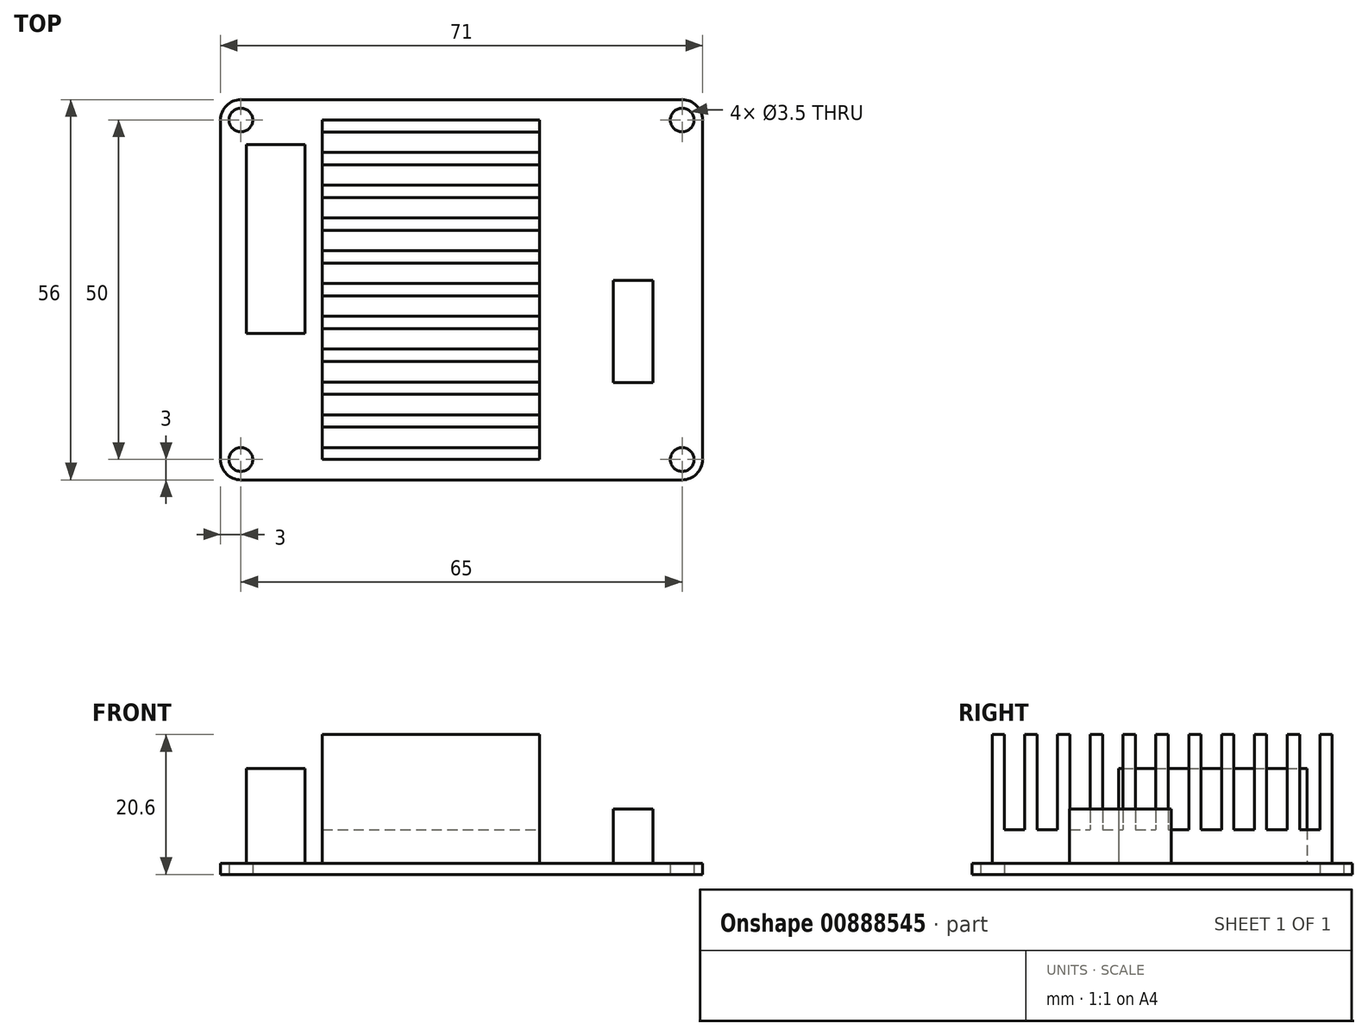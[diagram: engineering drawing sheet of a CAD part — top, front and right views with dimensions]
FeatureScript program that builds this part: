
annotation { "Feature Type Name" : "Feature", "Feature Type Description" : "" }
export const myFeature = defineFeature(function(context is Context, id is Id, definition is map)
    precondition{}
    {
        {
            var Q0;
            Q0=qCreatedBy(makeId("Top.planeOp"),FACE);
            var sketch = newSketch(context, id + "F0", { "sketchPlane" : qUnion([Q0])});
            skLineSegment(sketch, "E0.bottom", {"start": v(32.5, 28) * mm, "end": v(-32.5, 28) * mm});
            skLineSegment(sketch, "E0.top", {"start": v(32.5, -28) * mm, "end": v(-32.5, -28) * mm});
            skLineSegment(sketch, "E0.left", {"start": v(35.5, 25) * mm, "end": v(35.5, -25) * mm});
            skLineSegment(sketch, "E0.right", {"start": v(-35.5, 25) * mm, "end": v(-35.5, -25) * mm});
            skPoint(sketch, "E0.middle", {"position": v(0, 0) * mm});
            skPoint(sketch, "E1.visualSharp", {"position": v(-35.5, 28) * mm});
            skArc(sketch, "E1.filletArc", {"start": v(-32.5, 28) * mm, "mid": v(-34.62, 27.12) * mm, "end": v(-35.5, 25) * mm});
            skPoint(sketch, "E2.visualSharp", {"position": v(35.5, 28) * mm});
            skArc(sketch, "E2.filletArc", {"start": v(35.5, 25) * mm, "mid": v(34.62, 27.12) * mm, "end": v(32.5, 28) * mm});
            skPoint(sketch, "E3.visualSharp", {"position": v(35.5, -28) * mm});
            skArc(sketch, "E3.filletArc", {"start": v(32.5, -28) * mm, "mid": v(34.62, -27.12) * mm, "end": v(35.5, -25) * mm});
            skPoint(sketch, "E4.visualSharp", {"position": v(-35.5, -28) * mm});
            skArc(sketch, "E4.filletArc", {"start": v(-35.5, -25) * mm, "mid": v(-34.62, -27.12) * mm, "end": v(-32.5, -28) * mm});
            skCircle(sketch, "E5", {"center": v(-32.5, 25) * mm, "radius": 1.75 * mm});
            skCircle(sketch, "E6", {"center": v(-32.5, -25) * mm, "radius": 1.75 * mm});
            skCircle(sketch, "E7", {"center": v(32.5, -25) * mm, "radius": 1.75 * mm});
            skCircle(sketch, "E8", {"center": v(32.5, 25) * mm, "radius": 1.75 * mm});
            skSolve(sketch);
        }
        {
            var Q0;
            Q0 = qSketchRegion(id + "F0", true);
            extrude(context, id + "F1", {"entities" : qUnion([Q0]), "depth" : 1.6 * mm, "offsetDistance" : 25 * mm});
        }
        {
            var Q0;
            Q0=makeQuery(id+"F1.opExtrude","CAP_FACE",FACE,{"disambiguationData":[OSD([sQuery(id+"F0.wireOp",EDGE,"E0.bottom"),sQuery(id+"F0.wireOp",EDGE,"E0.top"),sQuery(id+"F0.wireOp",EDGE,"E0.left"),sQuery(id+"F0.wireOp",EDGE,"E0.right"),sQuery(id+"F0.wireOp",EDGE,"E1.filletArc"),sQuery(id+"F0.wireOp",EDGE,"E2.filletArc"),sQuery(id+"F0.wireOp",EDGE,"E3.filletArc"),sQuery(id+"F0.wireOp",EDGE,"E4.filletArc"),sQuery(id+"F0.wireOp",EDGE,"E5"),sQuery(id+"F0.wireOp",EDGE,"E6"),sQuery(id+"F0.wireOp",EDGE,"E7"),sQuery(id+"F0.wireOp",EDGE,"E8")])],"isStart":false});
            var sketch = newSketch(context, id + "F2", { "sketchPlane" : qUnion([Q0])});
            skLineSegment(sketch, "E9.bottom", {"start": v(28.21, -13.67) * mm, "end": v(22.37, -13.67) * mm});
            skLineSegment(sketch, "E9.top", {"start": v(28.21, 1.36) * mm, "end": v(22.37, 1.36) * mm});
            skLineSegment(sketch, "E9.left", {"start": v(28.21, -13.67) * mm, "end": v(28.21, 1.36) * mm});
            skLineSegment(sketch, "E9.right", {"start": v(22.37, -13.67) * mm, "end": v(22.37, 1.36) * mm});
            skPoint(sketch, "E9.middle", {"position": v(25.29, -6.16) * mm});
            skSolve(sketch);
        }
        {
            var Q0;
            Q0 = qSketchRegion(id + "F2", true);
            extrude(context, id + "F3", {"entities" : qUnion([Q0]), "operationType" : NewBodyOperationType.ADD, "depth" : 8 * mm, "offsetDistance" : 25 * mm});
        }
        {
            var Q0;
            Q0=makeQuery(id+"F1.opExtrude","CAP_FACE",FACE,{"disambiguationData":[OSD([sQuery(id+"F0.wireOp",EDGE,"E0.bottom"),sQuery(id+"F0.wireOp",EDGE,"E0.top"),sQuery(id+"F0.wireOp",EDGE,"E0.left"),sQuery(id+"F0.wireOp",EDGE,"E0.right"),sQuery(id+"F0.wireOp",EDGE,"E1.filletArc"),sQuery(id+"F0.wireOp",EDGE,"E2.filletArc"),sQuery(id+"F0.wireOp",EDGE,"E3.filletArc"),sQuery(id+"F0.wireOp",EDGE,"E4.filletArc"),sQuery(id+"F0.wireOp",EDGE,"E5"),sQuery(id+"F0.wireOp",EDGE,"E6"),sQuery(id+"F0.wireOp",EDGE,"E7"),sQuery(id+"F0.wireOp",EDGE,"E8")])],"isStart":false});
            var sketch = newSketch(context, id + "F4", { "sketchPlane" : qUnion([Q0])});
            skLineSegment(sketch, "E10.bottom", {"start": v(11.5, -25) * mm, "end": v(-20.5, -25) * mm});
            skLineSegment(sketch, "E10.top", {"start": v(11.5, 25) * mm, "end": v(-20.5, 25) * mm});
            skLineSegment(sketch, "E10.left", {"start": v(11.5, -25) * mm, "end": v(11.5, 25) * mm});
            skLineSegment(sketch, "E10.right", {"start": v(-20.5, -25) * mm, "end": v(-20.5, 25) * mm});
            skPoint(sketch, "E10.middle", {"position": v(-4.5, 0) * mm});
            skSolve(sketch);
        }
        {
            var Q0;
            Q0 = qSketchRegion(id + "F4", true);
            extrude(context, id + "F5", {"entities" : qUnion([Q0]), "operationType" : NewBodyOperationType.ADD, "depth" : 19 * mm, "offsetDistance" : 25 * mm});
        }
        {
            var Q0;
            Q0=makeQuery(id+"F5.opExtrude","SWEPT_FACE",FACE,{"disambiguationData":[OSD([sQuery(id+"F4.wireOp",EDGE,"E10.left")])]});
            var sketch = newSketch(context, id + "F6", { "sketchPlane" : qUnion([Q0])});
            skLineSegment(sketch, "E11.bottom", {"start": v(-23.24, 20.6) * mm, "end": v(-20.24, 20.6) * mm});
            skLineSegment(sketch, "E11.top", {"start": v(-23.24, 6.6) * mm, "end": v(-20.24, 6.6) * mm});
            skLineSegment(sketch, "E11.left", {"start": v(-23.24, 20.6) * mm, "end": v(-23.24, 6.6) * mm});
            skLineSegment(sketch, "E11.right", {"start": v(-20.24, 20.6) * mm, "end": v(-20.24, 6.6) * mm});
            skLineSegment(sketch, "E12.1.0.0", {"start": v(-18.4, 20.6) * mm, "end": v(-18.4, 6.6) * mm});
            skLineSegment(sketch, "E12.1.0.1", {"start": v(-18.4, 20.6) * mm, "end": v(-15.4, 20.6) * mm});
            skLineSegment(sketch, "E12.1.0.2", {"start": v(-15.4, 20.6) * mm, "end": v(-15.4, 6.6) * mm});
            skLineSegment(sketch, "E12.1.0.3", {"start": v(-18.4, 6.6) * mm, "end": v(-15.4, 6.6) * mm});
            skLineSegment(sketch, "E12.2.0.0", {"start": v(-13.58, 20.6) * mm, "end": v(-13.58, 6.6) * mm});
            skLineSegment(sketch, "E12.2.0.1", {"start": v(-13.58, 20.6) * mm, "end": v(-10.58, 20.6) * mm});
            skLineSegment(sketch, "E12.2.0.2", {"start": v(-10.58, 20.6) * mm, "end": v(-10.58, 6.6) * mm});
            skLineSegment(sketch, "E12.2.0.3", {"start": v(-13.58, 6.6) * mm, "end": v(-10.58, 6.6) * mm});
            skLineSegment(sketch, "E12.3.0.0", {"start": v(-8.75, 20.6) * mm, "end": v(-8.75, 6.6) * mm});
            skLineSegment(sketch, "E12.3.0.1", {"start": v(-8.75, 20.6) * mm, "end": v(-5.75, 20.6) * mm});
            skLineSegment(sketch, "E12.3.0.2", {"start": v(-5.75, 20.6) * mm, "end": v(-5.75, 6.6) * mm});
            skLineSegment(sketch, "E12.3.0.3", {"start": v(-8.75, 6.6) * mm, "end": v(-5.75, 6.6) * mm});
            skLineSegment(sketch, "E12.4.0.0", {"start": v(-3.92, 20.6) * mm, "end": v(-3.92, 6.6) * mm});
            skLineSegment(sketch, "E12.4.0.1", {"start": v(-3.92, 20.6) * mm, "end": v(-0.92, 20.6) * mm});
            skLineSegment(sketch, "E12.4.0.2", {"start": v(-0.92, 20.6) * mm, "end": v(-0.92, 6.6) * mm});
            skLineSegment(sketch, "E12.4.0.3", {"start": v(-3.92, 6.6) * mm, "end": v(-0.92, 6.6) * mm});
            skLineSegment(sketch, "E12.5.0.0", {"start": v(0.92, 20.6) * mm, "end": v(0.92, 6.6) * mm});
            skLineSegment(sketch, "E12.5.0.1", {"start": v(0.92, 20.6) * mm, "end": v(3.92, 20.6) * mm});
            skLineSegment(sketch, "E12.5.0.2", {"start": v(3.92, 20.6) * mm, "end": v(3.92, 6.6) * mm});
            skLineSegment(sketch, "E12.5.0.3", {"start": v(0.92, 6.6) * mm, "end": v(3.92, 6.6) * mm});
            skLineSegment(sketch, "E12.6.0.0", {"start": v(5.75, 20.6) * mm, "end": v(5.75, 6.6) * mm});
            skLineSegment(sketch, "E12.6.0.1", {"start": v(5.75, 20.6) * mm, "end": v(8.75, 20.6) * mm});
            skLineSegment(sketch, "E12.6.0.2", {"start": v(8.75, 20.6) * mm, "end": v(8.75, 6.6) * mm});
            skLineSegment(sketch, "E12.6.0.3", {"start": v(5.75, 6.6) * mm, "end": v(8.75, 6.6) * mm});
            skLineSegment(sketch, "E12.7.0.0", {"start": v(10.58, 20.6) * mm, "end": v(10.58, 6.6) * mm});
            skLineSegment(sketch, "E12.7.0.1", {"start": v(10.58, 20.6) * mm, "end": v(13.58, 20.6) * mm});
            skLineSegment(sketch, "E12.7.0.2", {"start": v(13.58, 20.6) * mm, "end": v(13.58, 6.6) * mm});
            skLineSegment(sketch, "E12.7.0.3", {"start": v(10.58, 6.6) * mm, "end": v(13.58, 6.6) * mm});
            skLineSegment(sketch, "E12.8.0.0", {"start": v(15.4, 20.6) * mm, "end": v(15.4, 6.6) * mm});
            skLineSegment(sketch, "E12.8.0.1", {"start": v(15.4, 20.6) * mm, "end": v(18.4, 20.6) * mm});
            skLineSegment(sketch, "E12.8.0.2", {"start": v(18.4, 20.6) * mm, "end": v(18.4, 6.6) * mm});
            skLineSegment(sketch, "E12.8.0.3", {"start": v(15.4, 6.6) * mm, "end": v(18.4, 6.6) * mm});
            skLineSegment(sketch, "E12.9.0.0", {"start": v(20.24, 20.6) * mm, "end": v(20.24, 6.6) * mm});
            skLineSegment(sketch, "E12.9.0.1", {"start": v(20.24, 20.6) * mm, "end": v(23.24, 20.6) * mm});
            skLineSegment(sketch, "E12.9.0.2", {"start": v(23.24, 20.6) * mm, "end": v(23.24, 6.6) * mm});
            skLineSegment(sketch, "E12.9.0.3", {"start": v(20.24, 6.6) * mm, "end": v(23.24, 6.6) * mm});
            skLineSegment(sketch, "E12.direction1", {"start": v(-23.24, 6.6) * mm, "end": v(-18.4, 6.6) * mm, "construction": true});
            skLineSegment(sketch, "E13", {"start": v(-23.24, 20.6) * mm, "end": v(-25, 20.6) * mm, "construction": true});
            skLineSegment(sketch, "E14", {"start": v(23.24, 20.6) * mm, "end": v(25, 20.6) * mm, "construction": true});
            skSolve(sketch);
        }
        {
            var Q0;
            Q0 = qSketchRegion(id + "F6", true);
            var Q1;
            Q1=makeQuery(id+"F5.opExtrude","SWEPT_FACE",FACE,{"disambiguationData":[OSD([sQuery(id+"F4.wireOp",EDGE,"E10.right")])]});
            extrude(context, id + "F7", {"entities" : qUnion([Q0]), "operationType" : NewBodyOperationType.REMOVE, "endBound" : BoundingType.UP_TO_SURFACE, "oppositeDirection" : true, "depth" : 25 * mm, "endBoundEntityFace" : qUnion([Q1]), "offsetDistance" : 25 * mm});
        }
        {
            var Q0;
            Q0=makeQuery(id+"F1.opExtrude","CAP_FACE",FACE,{"disambiguationData":[OSD([sQuery(id+"F0.wireOp",EDGE,"E0.bottom"),sQuery(id+"F0.wireOp",EDGE,"E0.top"),sQuery(id+"F0.wireOp",EDGE,"E0.left"),sQuery(id+"F0.wireOp",EDGE,"E0.right"),sQuery(id+"F0.wireOp",EDGE,"E1.filletArc"),sQuery(id+"F0.wireOp",EDGE,"E2.filletArc"),sQuery(id+"F0.wireOp",EDGE,"E3.filletArc"),sQuery(id+"F0.wireOp",EDGE,"E4.filletArc"),sQuery(id+"F0.wireOp",EDGE,"E5"),sQuery(id+"F0.wireOp",EDGE,"E6"),sQuery(id+"F0.wireOp",EDGE,"E7"),sQuery(id+"F0.wireOp",EDGE,"E8")])],"isStart":false});
            var sketch = newSketch(context, id + "F8", { "sketchPlane" : qUnion([Q0])});
            skLineSegment(sketch, "E15.bottom", {"start": v(-23.07, -6.43) * mm, "end": v(-31.67, -6.43) * mm});
            skLineSegment(sketch, "E15.top", {"start": v(-23.07, 21.37) * mm, "end": v(-31.67, 21.37) * mm});
            skLineSegment(sketch, "E15.left", {"start": v(-23.07, -6.43) * mm, "end": v(-23.07, 21.37) * mm});
            skLineSegment(sketch, "E15.right", {"start": v(-31.67, -6.43) * mm, "end": v(-31.67, 21.37) * mm});
            skPoint(sketch, "E15.middle", {"position": v(-27.37, 7.47) * mm});
            skSolve(sketch);
        }
        {
            var Q0;
            Q0 = qSketchRegion(id + "F8", true);
            extrude(context, id + "F9", {"entities" : qUnion([Q0]), "operationType" : NewBodyOperationType.ADD, "depth" : 14 * mm, "offsetDistance" : 25 * mm});
        }
    });
